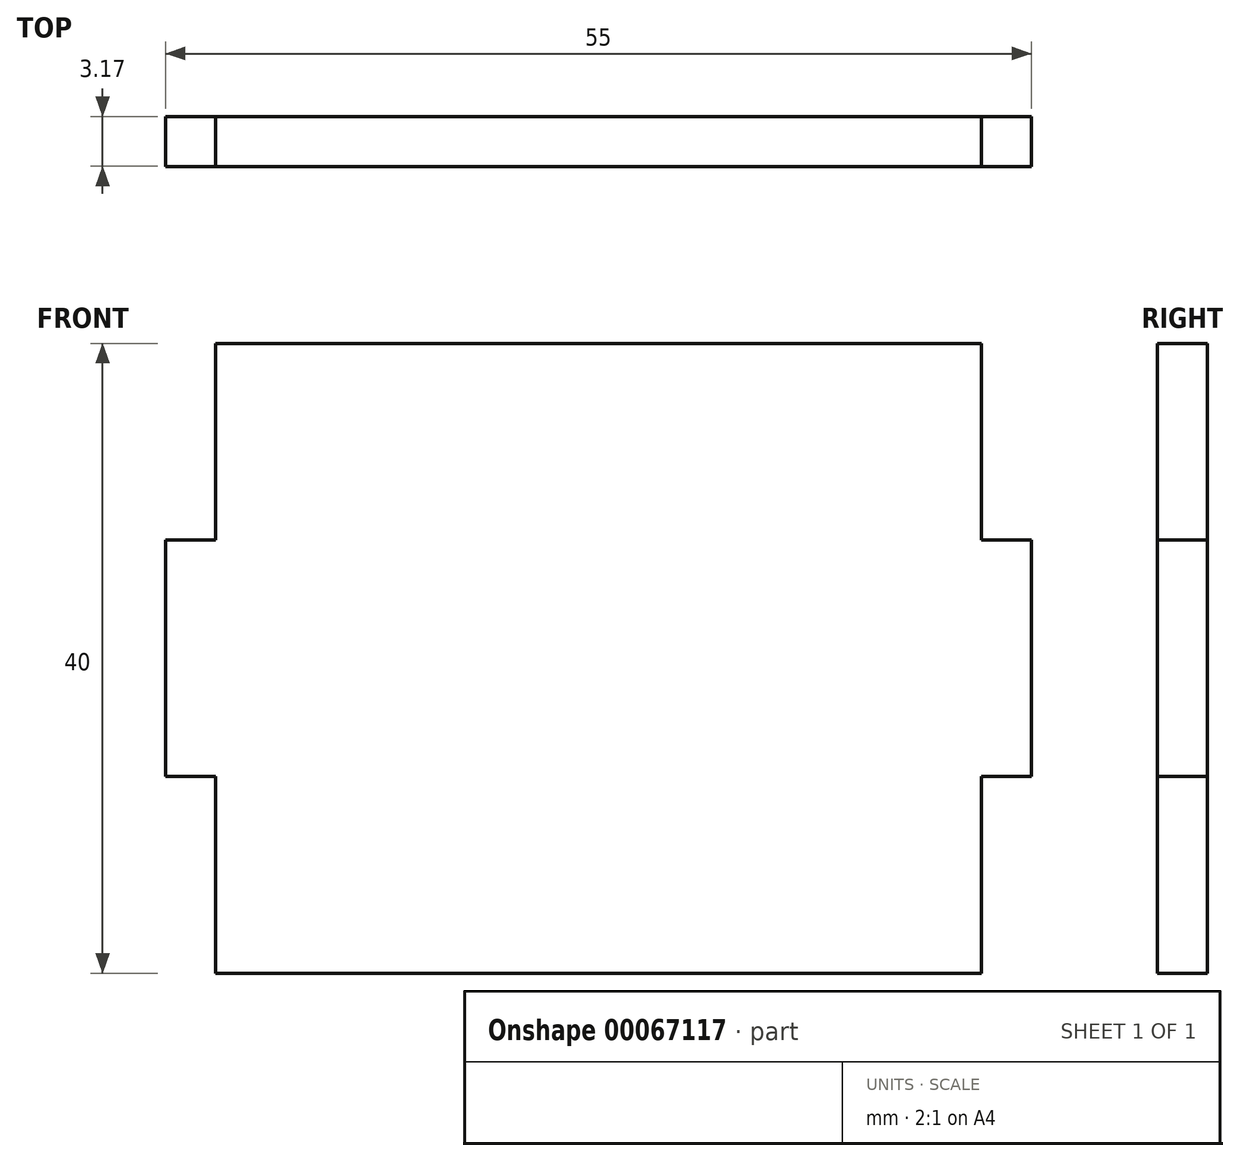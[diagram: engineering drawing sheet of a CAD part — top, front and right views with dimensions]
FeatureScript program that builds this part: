
annotation { "Feature Type Name" : "Feature", "Feature Type Description" : "" }
export const myFeature = defineFeature(function(context is Context, id is Id, definition is map)
    precondition{}
    {
        {
            var Q0;
            Q0=qCreatedBy(makeId("Front.planeOp"),FACE);
            var sketch = newSketch(context, id + "F0", { "sketchPlane" : qUnion([Q0])});
            skLineSegment(sketch, "E0.bottom", {"start": v(-24.33, 0) * mm, "end": v(24.32, 0) * mm});
            skLineSegment(sketch, "E0.top", {"start": v(-24.33, -40) * mm, "end": v(24.33, -40) * mm});
            skLineSegment(sketch, "E0.left", {"start": v(-24.32, 0) * mm, "end": v(-24.32, -40) * mm});
            skLineSegment(sketch, "E0.right", {"start": v(24.32, 0) * mm, "end": v(24.32, -40) * mm});
            skLineSegment(sketch, "E1.bottom", {"start": v(24.32, -12.5) * mm, "end": v(27.5, -12.5) * mm});
            skLineSegment(sketch, "E1.top", {"start": v(24.32, -27.5) * mm, "end": v(27.5, -27.5) * mm});
            skLineSegment(sketch, "E1.left", {"start": v(24.32, -12.5) * mm, "end": v(24.32, -27.5) * mm});
            skLineSegment(sketch, "E1.right", {"start": v(27.5, -12.5) * mm, "end": v(27.5, -27.5) * mm});
            skLineSegment(sketch, "E2", {"start": v(27.5, -12.5) * mm, "end": v(24.32, 0) * mm, "construction": true});
            skLineSegment(sketch, "E3", {"start": v(27.5, -27.5) * mm, "end": v(24.32, -40) * mm, "construction": true});
            skLineSegment(sketch, "E4.bottom", {"start": v(-24.32, -12.5) * mm, "end": v(-27.5, -12.5) * mm});
            skLineSegment(sketch, "E4.top", {"start": v(-24.32, -27.5) * mm, "end": v(-27.5, -27.5) * mm});
            skLineSegment(sketch, "E4.left", {"start": v(-24.32, -12.5) * mm, "end": v(-24.32, -27.5) * mm});
            skLineSegment(sketch, "E4.right", {"start": v(-27.5, -12.5) * mm, "end": v(-27.5, -27.5) * mm});
            skLineSegment(sketch, "E5.bottom", {"start": v(-10, -40) * mm, "end": v(10, -40) * mm});
            skLineSegment(sketch, "E5.top", {"start": v(-10, -46.35) * mm, "end": v(10, -46.35) * mm});
            skLineSegment(sketch, "E5.left", {"start": v(-10, -40) * mm, "end": v(-10, -46.35) * mm});
            skLineSegment(sketch, "E5.right", {"start": v(10, -40) * mm, "end": v(10, -46.35) * mm});
            skLineSegment(sketch, "E6", {"start": v(10, -46.35) * mm, "end": v(24.33, -40) * mm, "construction": true});
            skLineSegment(sketch, "E7", {"start": v(-10, -46.35) * mm, "end": v(-24.33, -40) * mm, "construction": true});
            skSolve(sketch);
        }
        {
            var Q0;
            {var subQ1=sQuery(id+"F0.wireOp",EDGE,"E0.bottom");Q0=makeQuery(id+"F0.imprint","IMPRINT",FACE,{"disambiguationData":[TD([[makeQuery(id+"F0.imprint","IMPRINT",EDGE,{"derivedFrom":subQ1}),-1.0]])]});}
            var Q1;
            Q1=makeQuery(id+"F0.imprint","IMPRINT",FACE,{"disambiguationData":[TD([[makeQuery(id+"F0.imprint","IMPRINT",EDGE,{"derivedFrom":sQuery(id+"F0.wireOp",EDGE,"E1.bottom")}),-1.0]])]});
            var Q2;
            Q2=makeQuery(id+"F0.imprint","IMPRINT",FACE,{"disambiguationData":[TD([[makeQuery(id+"F0.imprint","IMPRINT",EDGE,{"derivedFrom":sQuery(id+"F0.wireOp",EDGE,"E4.bottom")}),1.0]])]});
            var Q3;
            Q3=makeQuery(id+"F0.imprint","IMPRINT",FACE,{"disambiguationData":[TD([[makeQuery(id+"F0.imprint","IMPRINT",EDGE,{"derivedFrom":sQuery(id+"F0.wireOp",EDGE,"E5.bottom")}),-1.0]])]});
            extrude(context, id + "F1", {"entities" : qUnion([Q0, Q1, Q2, Q3]), "depth" : 3.17 * mm});
        }
    });
